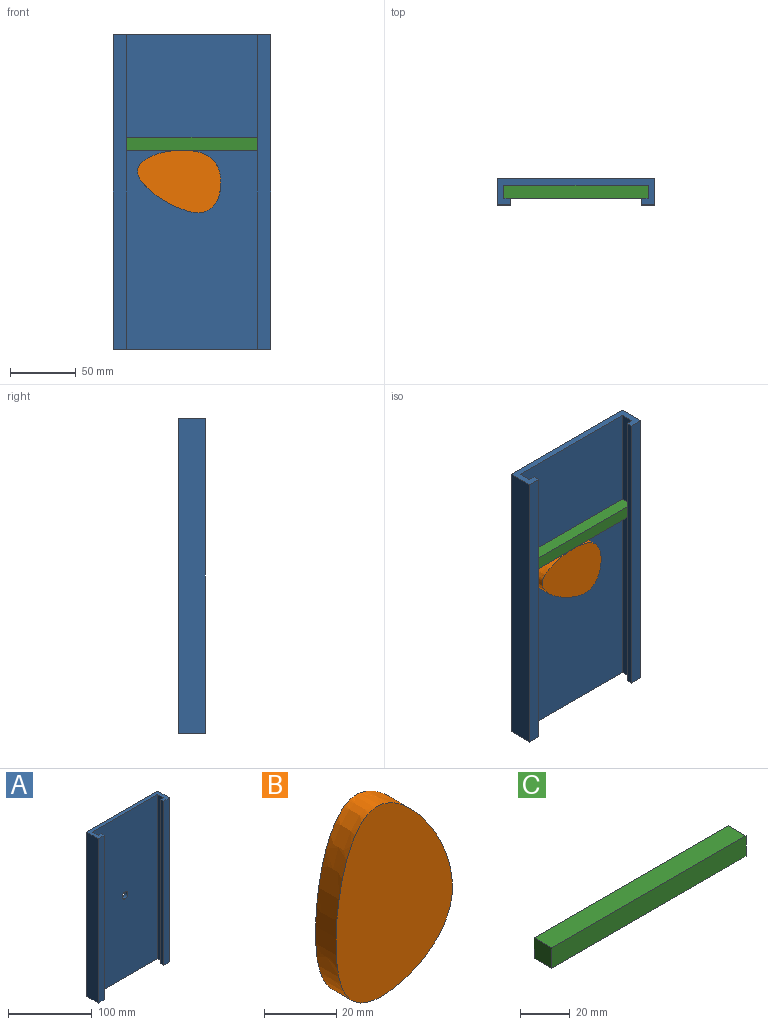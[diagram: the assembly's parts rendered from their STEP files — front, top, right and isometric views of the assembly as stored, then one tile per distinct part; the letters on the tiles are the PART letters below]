
ASSEMBLY  parts=3 mates=2
PART A: 15 faces, bbox 120x20x240 mm
  f0: plane 240x5mm, normal (1,0,0), area 1200mm2, adj f1,f3,f8,f13
  f1: plane 120x20mm, normal (0,0,-1), area 800mm2, adj f0,f2,f4,f5,f6,f7,f8,f9
  f2: plane 240x5mm, normal (-1,0,0), area 1200mm2, adj f1,f3,f6,f11
  f3: plane 120x20mm, normal (0,0,1), area 800mm2, adj f0,f2,f4,f5,f6,f7,f8,f9
  f4: plane 240x110mm, normal (0,-1,0), area 26321.5mm2, adj f1,f3,f5,f7,f14
  f5: plane 240x10mm, normal (-1,0,0), area 2400mm2, adj f1,f3,f4,f6
  f6: plane 240x5mm, normal (0,1,0), area 1200mm2, adj f1,f2,f3,f5
  f7: plane 240x10mm, normal (1,0,0), area 2400mm2, adj f1,f3,f4,f8
  f8: plane 240x5mm, normal (0,1,0), area 1200mm2, adj f0,f1,f3,f7
  f9: plane 240x120mm, normal (0,1,0), area 28721.5mm2, adj f1,f3,f10,f12,f14
  f10: plane 240x20mm, normal (1,0,0), area 4800mm2, adj f1,f3,f9,f11
  f11: plane 240x10mm, normal (0,-1,0), area 2400mm2, adj f1,f2,f3,f10
  f12: plane 240x20mm, normal (-1,0,0), area 4800mm2, adj f1,f3,f9,f13
  f13: plane 240x10mm, normal (0,-1,0), area 2400mm2, adj f0,f1,f3,f12
  f14: cylinder r=5mm len=10mm, axis (0,-1,0), area 157.1mm2, adj f4,f9
PART B: 5 faces, bbox 51x15x69 mm
  f0: plane 10x10mm, normal (0,1,0), area 78.5mm2, adj f1
  f1: cylinder r=5mm len=10mm, axis (0,-1,0), area 219.9mm2, adj f0,f4
  f2: extruded ~65.1x45.46mm, area 1405.8mm2, adj f3,f4
  f3: plane 69.02x51.05mm, normal (0,-1,0), area 2271.9mm2, adj f2
  f4: plane 69.02x51.05mm, normal (0,1,0), area 2193.4mm2, adj f1,f2
PART C: 6 faces, bbox 110x10x10 mm
  f0: plane 10x10mm, normal (1,0,0), area 100mm2, adj f1,f2,f4,f5
  f1: plane 110x10mm, normal (0,0,1), area 1100mm2, adj f0,f3,f4,f5
  f2: plane 110x10mm, normal (0,0,-1), area 1100mm2, adj f0,f3,f4,f5
  f3: plane 10x10mm, normal (-1,0,0), area 100mm2, adj f1,f2,f4,f5
  f4: plane 110x10mm, normal (0,1,0), area 1100mm2, adj f0,f1,f2,f3
  f5: plane 110x10mm, normal (0,-1,0), area 1100mm2, adj f0,f1,f2,f3
PLACE A at identity fixed
PLACE B rot(axis=(0,-1,0),65.8deg) t=(-49.19,0,-109.45)mm
PLACE C t=(0,0,-78.11)mm
MATE revolute A.f14 <-> B.f1  axis (0,1,0) through (0,7,0)mm
MATE slider A.f3 <-> C.f1  axis (0,0,1) through (-55,2,120)mm
